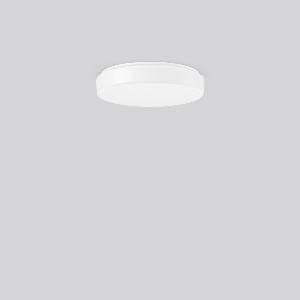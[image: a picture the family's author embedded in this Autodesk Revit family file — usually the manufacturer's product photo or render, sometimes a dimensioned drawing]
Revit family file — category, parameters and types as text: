
# Revit family: flat_polymero_kreis_slim_312084_002_2_76_1cdf
name_source: partatom
category: Lighting Fixtures
units: mm (PartAtom-declared; Revit-internal decimal feet)

## family parameters
Cut with Voids When Loaded = No
Host = Face
Light Source = No
Part Type = Normal
Room Calculation Point = No
Round Connector Dimension = Use Diameter
Shared = No

## types (1)
- FLAT POLYMERO KREIS SLIM (1 x LED Modul 830, 1300 lm, 3000)
    Apparent Load = 12 VA
    CIE Flux Codes = 43 73 92 88 100
    Color Rendering = 80
    Color Temperature = 3000
    Default Elevation = 1800 mm
    Description = Series: FLAT POLYMERO KREIS SLIM
Flat decorative round LED surface-mounted luminaire. Base: metal, powder-coated. Diffuser made of plastic (polycarbonate), opal, shockproof. Diffuser fastening: patented push system. Suitable for Ceiling mounting, Wall (surface). 
Colour: white
Diameter: 300 mm
Height: 65 mm
Lamp: LED exchangeable
Socket: without socket
Colour temperature: 3000K
Colour rendering index (CRI): 83
System power: 12 W
Rated luminous flux: 1300 lm
Luminous efficiency: 108 lm/W
Control gear: AC power, DALI dimmable
Protection class: I
Type of protection: IP 40
    Height = 65 mm
    Lamp = 1 x LED Modul 830
    Lamp Light Flux = 1300 lm
    Lamp count = 1
    Length = 300 mm
    Lifetime = 50000 h
    Luminous efficacy = 108 lm/W
    Manufacturer = RZB
    ModVariant = No
    Model = 312084.002.2.76
    Mounting Place = Ceiling, Wall
    Mounting Type = Surface mounted
    Number of Poles = 1
    OnlyDefault = Yes
    Power Factor = 1
    Product Name = FLAT POLYMERO KREIS SLIM
    Product group = Surface mounted ceiling and wall luminaires
    ProductGroupID = 305
    Protection Class = Protection class I
    Protection Degree = IP 40
    RLX_Detail_Level = 1
    RLX_Emergency_Light_Flux = 0 lm
    RLX_Emergency_Type = 0
    RLX_Emergency_Type_DB = No
    RlxData = <blob elided: 54185 chars, md5=9898d593>
    Socket = socket
    Standby Power = 0 W
    System Light Flux = 1300 lm
    System Power = 12 W
    Type Comments = Product without accessories
    Type Image = 312084.002.jpg
    URL = http://relux.com
    VarID = ---
    Voltage = 230 V
    Voltage Range = 220-240 V
    Weight = 0.00 kg
    Width = 0 mm  [stored 0 ft]

note: [stored X ft] marks values corroborated as IEEE doubles in the binary element streams (Revit-internal decimal feet)

## geometry (parser evidence)
native form markers: Blend x4, Sweep x13
no freeform markers — native parametric forms only
